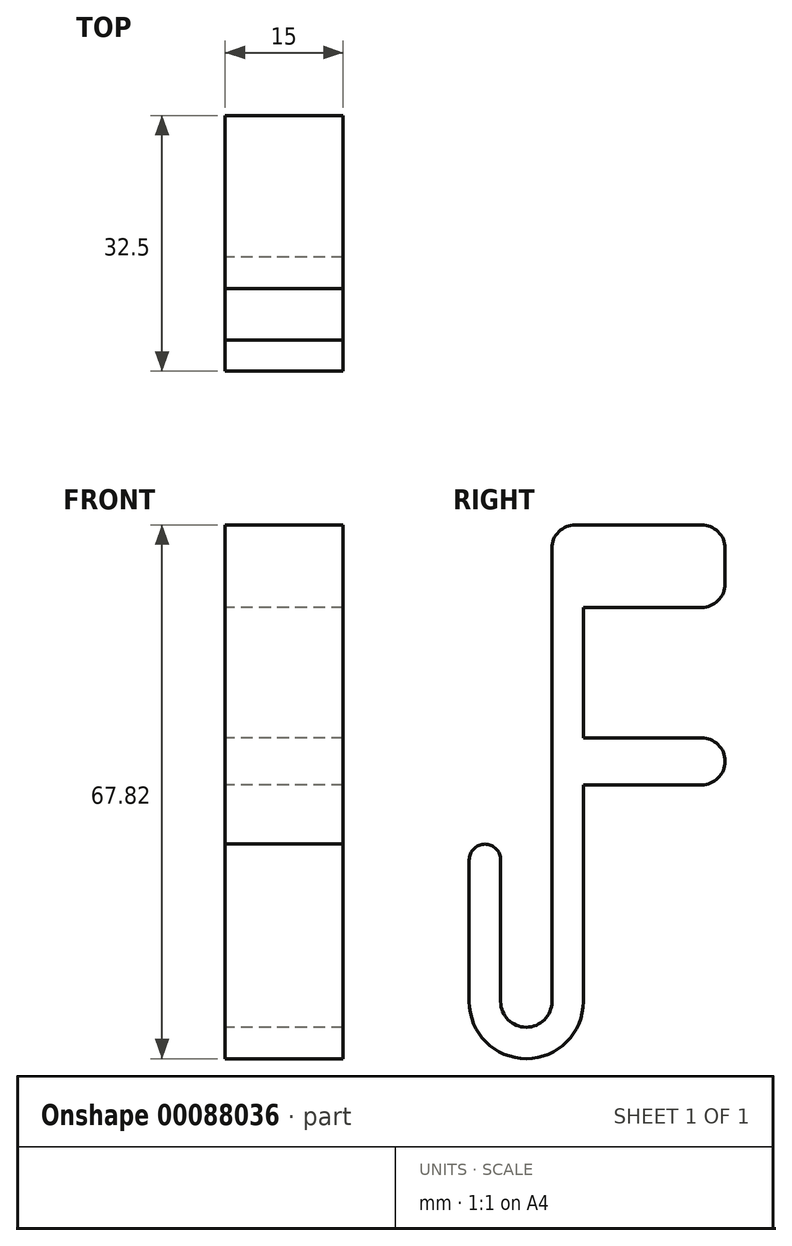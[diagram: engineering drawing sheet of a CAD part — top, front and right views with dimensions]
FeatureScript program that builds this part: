
annotation { "Feature Type Name" : "Feature", "Feature Type Description" : "" }
export const myFeature = defineFeature(function(context is Context, id is Id, definition is map)
    precondition{}
    {
        {
            var Q0;
            Q0=qCreatedBy(makeId("Right.planeOp"),FACE);
            var sketch = newSketch(context, id + "F0", { "sketchPlane" : qUnion([Q0])});
            skLineSegment(sketch, "E0", {"start": v(0, 30.37) * mm, "end": v(-18, 30.37) * mm});
            skLineSegment(sketch, "E1", {"start": v(-18, 30.37) * mm, "end": v(-18, 13.82) * mm});
            skLineSegment(sketch, "E2", {"start": v(-18, 13.82) * mm, "end": v(0, 13.82) * mm});
            skLineSegment(sketch, "E3", {"start": v(0, 13.82) * mm, "end": v(0, 7.82) * mm});
            skLineSegment(sketch, "E4", {"start": v(0, 7.82) * mm, "end": v(-18, 7.82) * mm});
            skLineSegment(sketch, "E5", {"start": v(-18, 7.82) * mm, "end": v(-18, -19.7) * mm});
            skLineSegment(sketch, "E6", {"start": v(0, 30.37) * mm, "end": v(0, 40.87) * mm});
            skLineSegment(sketch, "E7", {"start": v(0, 40.87) * mm, "end": v(-22, 40.87) * mm});
            skLineSegment(sketch, "E8", {"start": v(-22, 40.87) * mm, "end": v(-22, -19.7) * mm});
            skArc(sketch, "E9", {"start": v(-28.5, -19.7) * mm, "mid": v(-25.25, -22.95) * mm, "end": v(-22, -19.7) * mm});
            skArc(sketch, "E10", {"start": v(-32.5, -19.7) * mm, "mid": v(-25.25, -26.95) * mm, "end": v(-18, -19.7) * mm});
            skLineSegment(sketch, "E11", {"start": v(-28.5, -19.7) * mm, "end": v(-28.5, -1.7) * mm});
            skLineSegment(sketch, "E12", {"start": v(-32.5, -19.7) * mm, "end": v(-32.5, -1.7) * mm});
            skArc(sketch, "E13", {"start": v(-28.5, -1.7) * mm, "mid": v(-30.5, 0.3) * mm, "end": v(-32.5, -1.7) * mm});
            skSolve(sketch);
        }
        {
            var Q0;
            Q0 = qSketchRegion(id + "F0", true);
            extrude(context, id + "F1", {"entities" : qUnion([Q0]), "depth" : 15 * mm});
        }
        {
            var Q0;
            Q0=makeQuery(id+"F1.opExtrude","SWEPT_EDGE",EDGE,{"disambiguationData":[OSD([sQuery(id+"F0.wireOp",EDGE,"E0"),sQuery(id+"F0.wireOp",EDGE,"E6")])]});
            var Q1;
            Q1=makeQuery(id+"F1.opExtrude","SWEPT_EDGE",EDGE,{"disambiguationData":[OSD([sQuery(id+"F0.wireOp",EDGE,"E2"),sQuery(id+"F0.wireOp",EDGE,"E3")])]});
            var Q2;
            Q2=makeQuery(id+"F1.opExtrude","SWEPT_EDGE",EDGE,{"disambiguationData":[OSD([sQuery(id+"F0.wireOp",EDGE,"E6"),sQuery(id+"F0.wireOp",EDGE,"E7")])]});
            var Q3;
            Q3=makeQuery(id+"F1.opExtrude","SWEPT_EDGE",EDGE,{"disambiguationData":[OSD([sQuery(id+"F0.wireOp",EDGE,"E3"),sQuery(id+"F0.wireOp",EDGE,"E4")])]});
            var Q4;
            Q4=makeQuery(id+"F1.opExtrude","SWEPT_EDGE",EDGE,{"disambiguationData":[OSD([sQuery(id+"F0.wireOp",EDGE,"E7"),sQuery(id+"F0.wireOp",EDGE,"E8")])]});
            fillet(context, id + "F2", {"entities" : qUnion([Q0, Q1, Q2, Q3, Q4]), "radius" : 3 * mm, "tangentPropagation" : true, "allowEdgeOverflow" : false});
        }
    });
